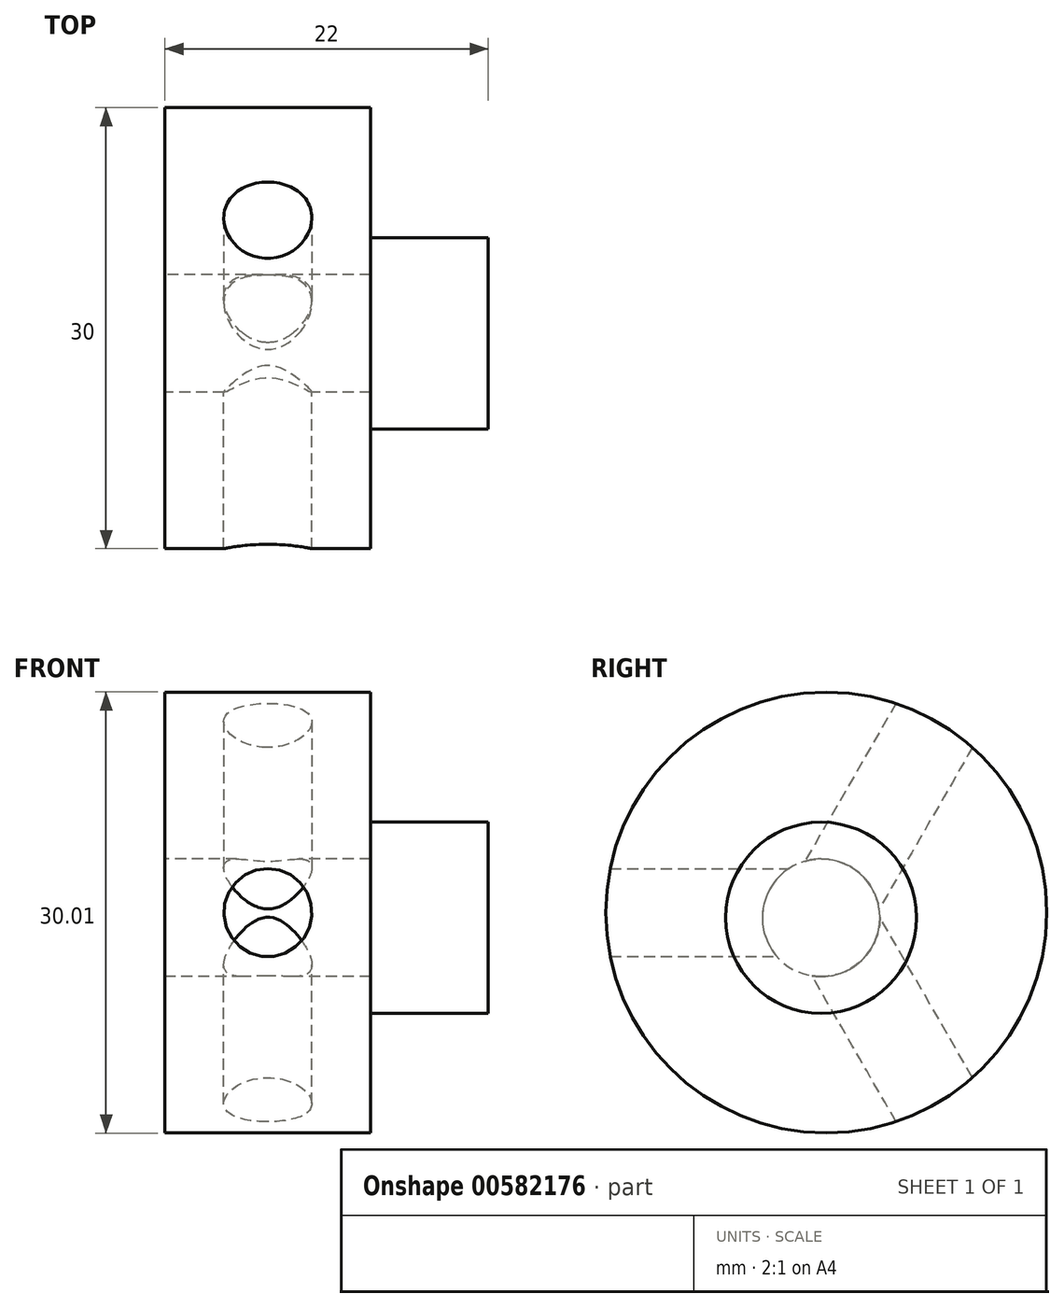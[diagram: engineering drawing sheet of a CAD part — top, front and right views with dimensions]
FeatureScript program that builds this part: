
annotation { "Feature Type Name" : "Feature", "Feature Type Description" : "" }
export const myFeature = defineFeature(function(context is Context, id is Id, definition is map)
    precondition{}
    {
        {
            var Q0;
            Q0=qCreatedBy(makeId("Right.planeOp"),FACE);
            var sketch = newSketch(context, id + "F0", { "sketchPlane" : qUnion([Q0])});
            skCircle(sketch, "E0", {"center": v(-77.78, 77.78) * mm, "radius": 4 * mm});
            skLineSegment(sketch, "E1", {"start": v(0, 0) * mm, "end": v(-105, 105) * mm, "construction": true});
            skLineSegment(sketch, "E2", {"start": v(0, 0) * mm, "end": v(0, 148.5) * mm, "construction": true});
            skCircle(sketch, "E3", {"center": v(-77.43, 78.14) * mm, "radius": 15 * mm});
            skLineSegment(sketch, "E4", {"start": v(-77.78, 77.78) * mm, "end": v(-77.43, 78.14) * mm, "construction": true});
            skSolve(sketch);
        }
        {
            var Q0;
            Q0=qSketchRegion(id+"F0",true);
            extrude(context, id + "F1", {"entities" : qUnion([Q0]), "depth" : 14 * mm, "offsetDistance" : 25 * mm});
        }
        {
            var Q0;
            Q0=makeQuery(id+"F1.opExtrude","SWEPT_FACE",FACE,{"disambiguationData":[OSD([sQuery(id+"F0.wireOp",EDGE,"E3")])]});
            cPlane(context, id + "F2", {"entities" : qUnion([Q0]), "cplaneType" : CPlaneType.LINE_ANGLE, "offset" : 25 * mm, "angle" : 0 * degree, "width" : 150 * mm, "height" : 150 * mm});
        }
        {
            var Q0;
            Q0=qCreatedBy(id+"F2.planeOp",FACE);
            var sketch = newSketch(context, id + "F3", { "sketchPlane" : qUnion([Q0])});
            skCircle(sketch, "E5", {"center": v(7, 78.14) * mm, "radius": 3 * mm});
            skLineSegment(sketch, "E6", {"start": v(0, 78.14) * mm, "end": v(14, 78.14) * mm, "construction": true});
            skSolve(sketch);
        }
        {
            var Q0;
            Q0=qSketchRegion(id+"F3",true);
            extrude(context, id + "F4", {"entities" : qUnion([Q0]), "depth" : 25 * mm, "offsetDistance" : 25 * mm});
        }
        {
            var Q0;
            Q0=makeQuery(id+"F4.opExtrude","SWEPT_BODY",BODY,{"disambiguationData":[OSD([sQuery(id+"F3.wireOp",EDGE,"E5")])]});
            var Q1;
            Q1=makeQuery(id+"F1.opExtrude","CAP_EDGE",EDGE,{"disambiguationData":[OSD([sQuery(id+"F0.wireOp",EDGE,"E3")])],"isStart":true});
            circularPattern(context, id + "F5", {"entities" : qUnion([Q0]), "axis" : qUnion([Q1]), "angle" : 360 * degree, "instanceCount" : 3, "equalSpace" : true});
        }
        {
            var Q0;
            Q0=makeQuery(id+"F4.opExtrude","SWEPT_BODY",BODY,{"disambiguationData":[OSD([sQuery(id+"F3.wireOp",EDGE,"E5")])]});
            var Q1;
            Q1=makeQuery(id+"F5.opPattern","COPY",BODY,{"derivedFrom":makeQuery(id+"F4.opExtrude","SWEPT_BODY",BODY,{"disambiguationData":[OSD([sQuery(id+"F3.wireOp",EDGE,"E5")])]}),"instanceName":"1"});
            var Q2;
            Q2=makeQuery(id+"F5.opPattern","COPY",BODY,{"derivedFrom":makeQuery(id+"F4.opExtrude","SWEPT_BODY",BODY,{"disambiguationData":[OSD([sQuery(id+"F3.wireOp",EDGE,"E5")])]}),"instanceName":"2"});
            var Q3;
            Q3=makeQuery(id+"F1.opExtrude","SWEPT_BODY",BODY,{"disambiguationData":[OSD([sQuery(id+"F0.wireOp",EDGE,"E0"),sQuery(id+"F0.wireOp",EDGE,"E3")])]});
            booleanBodies(context, id + "F6", {"operationType" : BooleanOperationType.SUBTRACTION, "tools" : qUnion([Q0, Q1, Q2]), "targets" : qUnion([Q3])});
        }
        {
            var Q0;
            Q0=makeQuery(id+"F1.opExtrude","CAP_FACE",FACE,{"disambiguationData":[OSD([sQuery(id+"F0.wireOp",EDGE,"E0"),sQuery(id+"F0.wireOp",EDGE,"E3")])],"isStart":false});
            var sketch = newSketch(context, id + "F7", { "sketchPlane" : qUnion([Q0])});
            skCircle(sketch, "E7", {"center": v(-77.78, 77.78) * mm, "radius": 6.5 * mm});
            skSolve(sketch);
        }
        {
            var Q0;
            Q0=qSketchRegion(id+"F7",true);
            extrude(context, id + "F8", {"entities" : qUnion([Q0]), "operationType" : NewBodyOperationType.ADD, "depth" : 8 * mm, "offsetDistance" : 25 * mm});
        }
    });
